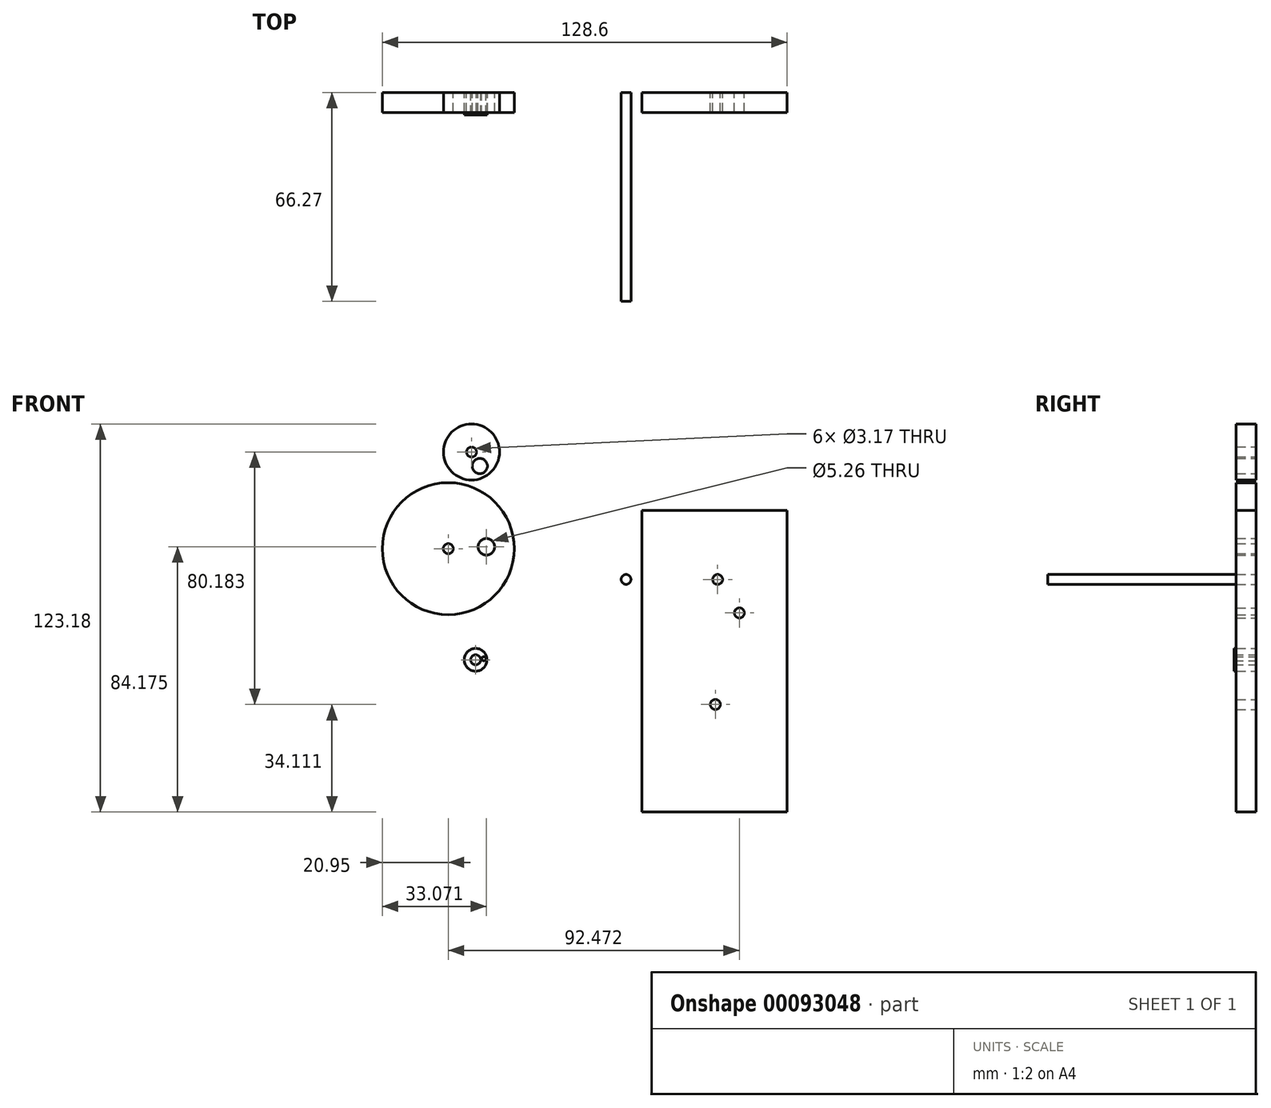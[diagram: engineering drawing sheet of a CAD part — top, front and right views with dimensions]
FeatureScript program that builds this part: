
annotation { "Feature Type Name" : "Feature", "Feature Type Description" : "" }
export const myFeature = defineFeature(function(context is Context, id is Id, definition is map)
    precondition{}
    {
        {
            var Q0;
            Q0=qCreatedBy(makeId("Front.planeOp"),FACE);
            var sketch = newSketch(context, id + "F0", { "sketchPlane" : qUnion([Q0])});
            skCircle(sketch, "E0", {"center": v(0, 0) * mm, "radius": 1.56 * mm});
            skLineSegment(sketch, "E1.bottom", {"start": v(5.02, 21.97) * mm, "end": v(51.18, 21.97) * mm});
            skLineSegment(sketch, "E1.top", {"start": v(5.02, -73.83) * mm, "end": v(51.18, -73.83) * mm});
            skLineSegment(sketch, "E1.left", {"start": v(5.02, 21.97) * mm, "end": v(5.02, -73.83) * mm});
            skLineSegment(sketch, "E1.right", {"start": v(51.18, 21.97) * mm, "end": v(51.18, -73.83) * mm});
            skCircle(sketch, "E2", {"center": v(-49.08, 40.46) * mm, "radius": 8.9 * mm});
            skCircle(sketch, "E3", {"center": v(-56.47, 9.77) * mm, "radius": 20.96 * mm});
            skCircle(sketch, "E4", {"center": v(-49.08, 40.46) * mm, "radius": 1.59 * mm});
            skCircle(sketch, "E5", {"center": v(-56.47, 9.77) * mm, "radius": 1.59 * mm});
            skCircle(sketch, "E6", {"center": v(29.1, 0) * mm, "radius": 1.59 * mm});
            skCircle(sketch, "E7", {"center": v(36, -10.65) * mm, "radius": 1.59 * mm});
            skCircle(sketch, "E8", {"center": v(28.37, -39.72) * mm, "radius": 1.59 * mm});
            skCircle(sketch, "E9", {"center": v(-44.35, 10.34) * mm, "radius": 2.63 * mm});
            skCircle(sketch, "E10", {"center": v(-46.44, 36.01) * mm, "radius": 2.41 * mm});
            skSolve(sketch);
        }
        {
            var Q0;
            Q0=makeQuery(id+"F0.imprint","IMPRINT",FACE,{"disambiguationData":[TD([[makeQuery(id+"F0.imprint","IMPRINT",EDGE,{"derivedFrom":sQuery(id+"F0.wireOp",EDGE,"E0")}),1.0]])]});
            extrude(context, id + "F1", {"entities" : qUnion([Q0]), "depth" : 66.27 * mm});
        }
        {
            var Q0;
            Q0 = qSketchRegion(id + "F0", true);
            extrude(context, id + "F2", {"entities" : qUnion([Q0]), "operationType" : NewBodyOperationType.ADD, "depth" : 6.35 * mm});
        }
        {
            var Q0;
            Q0=qCreatedBy(makeId("Front.planeOp"),FACE);
            var sketch = newSketch(context, id + "F3", { "sketchPlane" : qUnion([Q0])});
            skCircle(sketch, "E11", {"center": v(-47.77, -25.53) * mm, "radius": 3.6 * mm});
            skCircle(sketch, "E12", {"center": v(-47.77, -25.53) * mm, "radius": 1.59 * mm});
            skCircle(sketch, "E13", {"center": v(-45.17, -25.16) * mm, "radius": 0.65 * mm});
            skSolve(sketch);
        }
        {
            var Q0;
            Q0=makeQuery(id+"F3.imprint","IMPRINT",FACE,{"disambiguationData":[TD([[makeQuery(id+"F3.imprint","IMPRINT",EDGE,{"derivedFrom":sQuery(id+"F3.wireOp",EDGE,"E11")}),1.0]])]});
            extrude(context, id + "F4", {"entities" : qUnion([Q0]), "operationType" : NewBodyOperationType.ADD, "depth" : 7.1 * mm});
        }
    });
